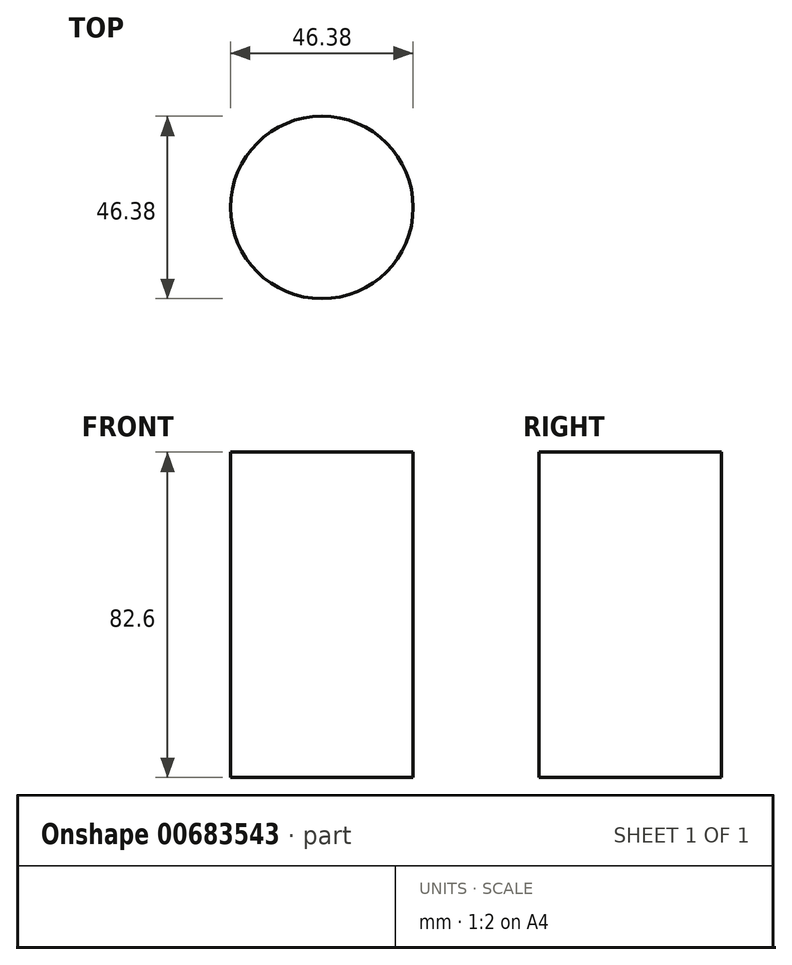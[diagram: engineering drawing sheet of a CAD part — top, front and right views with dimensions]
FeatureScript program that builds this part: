
annotation { "Feature Type Name" : "Feature", "Feature Type Description" : "" }
export const myFeature = defineFeature(function(context is Context, id is Id, definition is map)
    precondition{}
    {
        {
            var Q0;
            Q0=qCreatedBy(makeId("Top.planeOp"),FACE);
            var sketch = newSketch(context, id + "F0", { "sketchPlane" : qUnion([Q0])});
            skCircle(sketch, "E0", {"center": v(-35.59, -42.2) * mm, "radius": 23.19 * mm});
            skSolve(sketch);
        }
        {
            var Q0;
            Q0=makeQuery(id+"F0.imprint","IMPRINT",FACE,{"disambiguationData":[TD([[makeQuery(id+"F0.imprint","IMPRINT",EDGE,{"derivedFrom":sQuery(id+"F0.wireOp",EDGE,"E0")}),1.0]])]});
            extrude(context, id + "F1", {"entities" : qUnion([Q0]), "depth" : 82.6 * mm, "offsetDistance" : 25.4 * mm});
        }
    });
